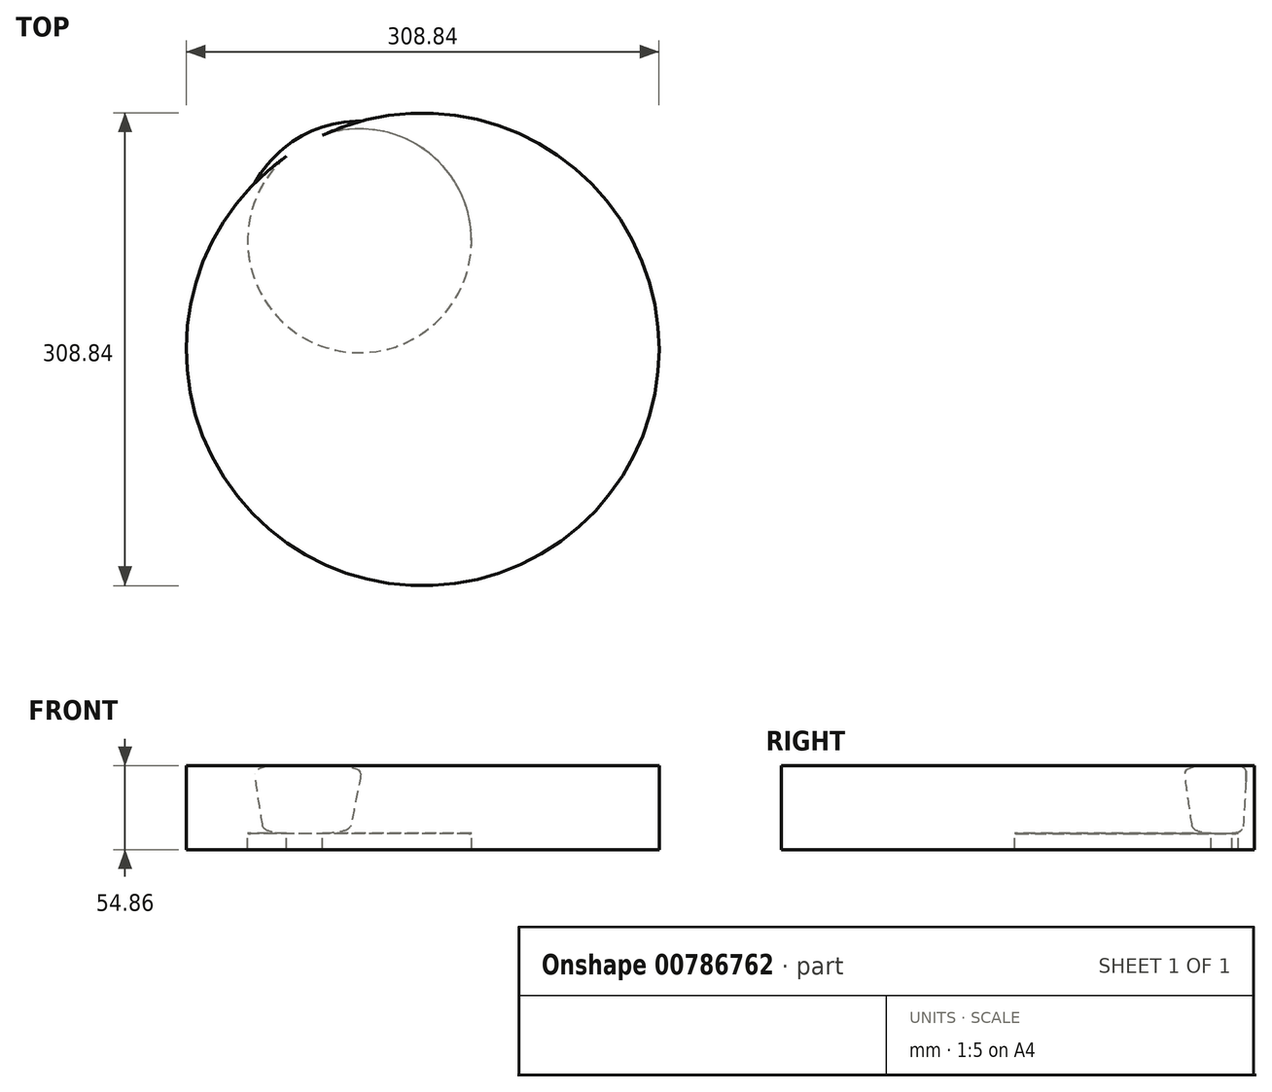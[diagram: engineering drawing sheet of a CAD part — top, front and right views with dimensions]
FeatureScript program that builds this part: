
annotation { "Feature Type Name" : "Feature", "Feature Type Description" : "" }
export const myFeature = defineFeature(function(context is Context, id is Id, definition is map)
    precondition{}
    {
        {
            var Q0;
            Q0=qCreatedBy(makeId("Top.planeOp"),FACE);
            var sketch = newSketch(context, id + "F0", { "sketchPlane" : qUnion([Q0])});
            skCircle(sketch, "E0", {"center": v(0, 0) * mm, "radius": 76.14 * mm});
            skSolve(sketch);
        }
        {
            var Q0;
            Q0=makeQuery(id+"F0.imprint","IMPRINT",FACE,{"disambiguationData":[TD([[makeQuery(id+"F0.imprint","IMPRINT",EDGE,{"derivedFrom":sQuery(id+"F0.wireOp",EDGE,"E0")}),1.0]])]});
            extrude(context, id + "F1", {"entities" : qUnion([Q0]), "depth" : 44.45 * mm, "offsetDistance" : 25.4 * mm, "hasDraft" : true, "draftAngle" : 3 * degree});
        }
        {
            var Q0;
            Q0=makeQuery(id+"F1.opExtrude","CAP_FACE",FACE,{"disambiguationData":[OSD([sQuery(id+"F0.wireOp",EDGE,"E0")])],"isStart":false});
            var Q1;
            Q1=makeQuery(id+"F1.opExtrude","SWEPT_FACE",FACE,{"disambiguationData":[OSD([sQuery(id+"F0.wireOp",EDGE,"E0")])]});
            fillet(context, id + "F2", {"entities" : qUnion([Q0, Q1]), "radius" : 5.08 * mm, "tangentPropagation" : true, "allowEdgeOverflow" : false});
        }
        {
            var Q0;
            Q0=makeQuery(id+"F1.opExtrude","CAP_FACE",FACE,{"disambiguationData":[OSD([sQuery(id+"F0.wireOp",EDGE,"E0")])],"isStart":false});
            var sketch = newSketch(context, id + "F3", { "sketchPlane" : qUnion([Q0])});
            skCircle(sketch, "E1", {"center": v(41.17, -70.9) * mm, "radius": 154.42 * mm});
            skSolve(sketch);
        }
        {
            var Q0;
            {var subQ0=sQuery(id+"F3.wireOp",EDGE,"E1");var subQ1=sQuery(id+"F0.wireOp",EDGE,"E0");var subQ2=makeQuery(id+"F2.opFillet","BLEND_EDGE",EDGE,{"blendedFrom":[makeQuery(id+"F1.opExtrude","CAP_EDGE",EDGE,{"disambiguationData":[OSD([subQ1])],"isStart":false}),makeQuery(id+"F1.opExtrude","CAP_FACE",FACE,{"disambiguationData":[OSD([subQ1])],"isStart":false})],"blendedInto":[makeQuery(id+"F1.opExtrude","CAP_FACE",FACE,{"disambiguationData":[OSD([subQ1])],"isStart":false})]});var subQ3=makeQuery(id+"F3.imprint","INTERSECT",VERTEX,{"disambiguationData":[OD(0.0)],"derivedFrom":[subQ2,subQ0]});Q0=makeQuery(id+"F3.imprint","IMPRINT",FACE,{"disambiguationData":[TD([[makeQuery(id+"F3.imprint","IMPRINT",EDGE,{"disambiguationData":[TD([[subQ3,-1.0]])],"derivedFrom":subQ0}),1.0]])]});}
            extrude(context, id + "F4", {"entities" : qUnion([Q0]), "operationType" : NewBodyOperationType.ADD, "oppositeDirection" : true, "depth" : 54.86 * mm, "offsetDistance" : 25.4 * mm});
        }
    });
